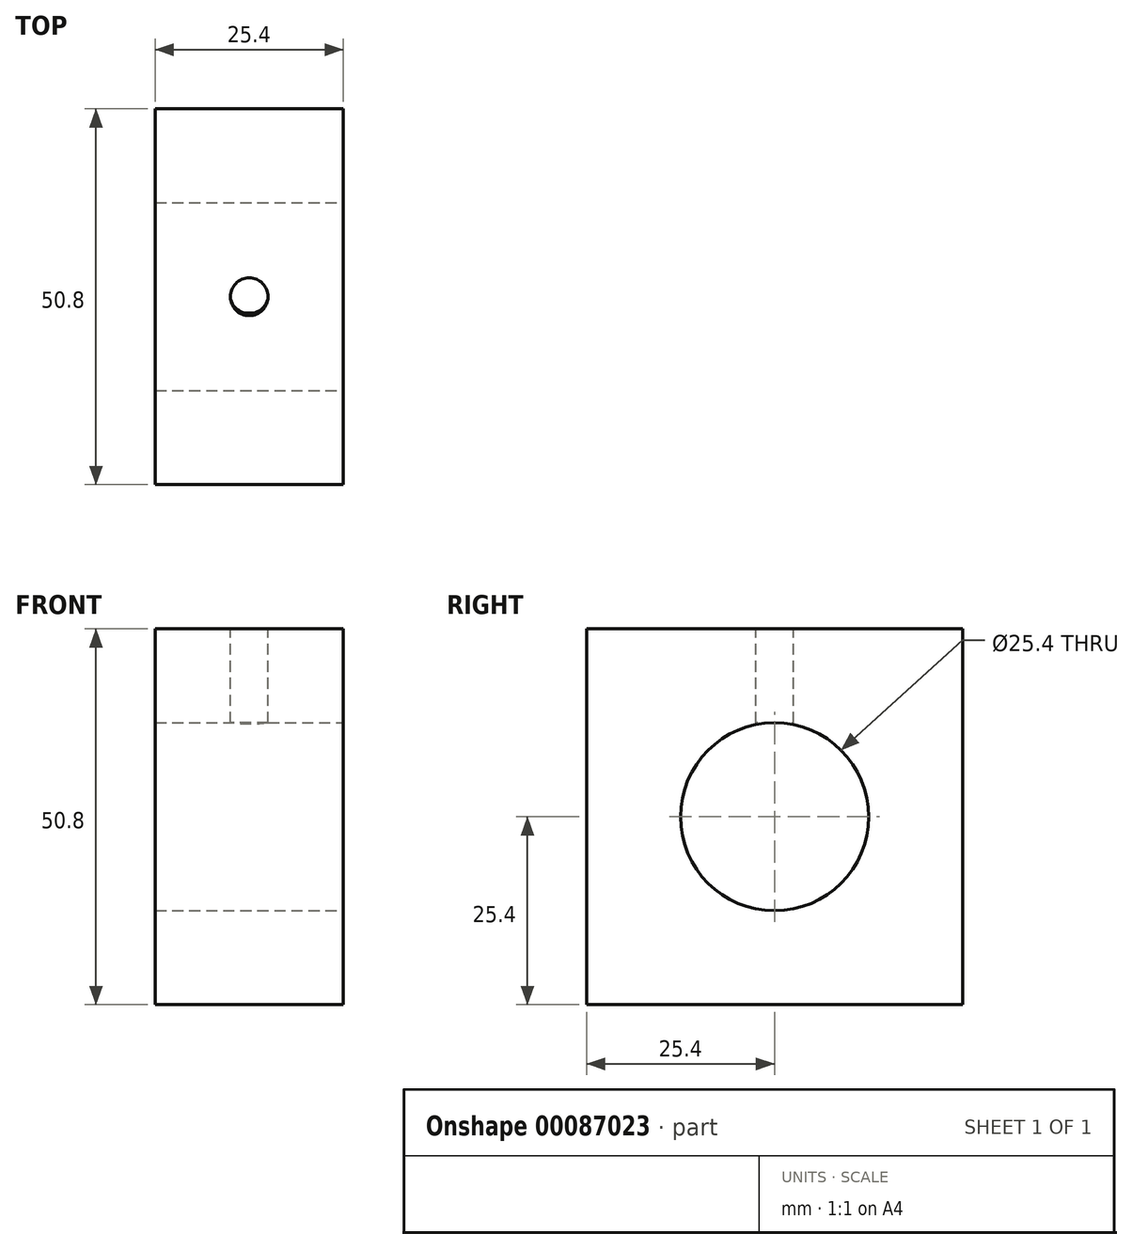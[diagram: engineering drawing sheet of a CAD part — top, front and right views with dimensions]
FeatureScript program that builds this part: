
annotation { "Feature Type Name" : "Feature", "Feature Type Description" : "" }
export const myFeature = defineFeature(function(context is Context, id is Id, definition is map)
    precondition{}
    {
        {
            var Q0;
            Q0=qCreatedBy(makeId("Front.planeOp"),FACE);
            var sketch = newSketch(context, id + "F0", { "sketchPlane" : qUnion([Q0])});
            skLineSegment(sketch, "E0.bottom", {"start": v(0, 0) * mm, "end": v(25.4, 0) * mm});
            skLineSegment(sketch, "E0.top", {"start": v(0, 50.8) * mm, "end": v(25.4, 50.8) * mm});
            skLineSegment(sketch, "E0.left", {"start": v(0, 0) * mm, "end": v(0, 50.8) * mm});
            skLineSegment(sketch, "E0.right", {"start": v(25.4, 0) * mm, "end": v(25.4, 50.8) * mm});
            skSolve(sketch);
        }
        {
            var Q0;
            Q0 = qSketchRegion(id + "F0", true);
            extrude(context, id + "F1", {"entities" : qUnion([Q0]), "depth" : 50.8 * mm});
        }
        {
            var Q0;
            Q0=makeQuery(id+"F1.opExtrude","SWEPT_FACE",FACE,{"disambiguationData":[OSD([sQuery(id+"F0.wireOp",EDGE,"E0.right")])]});
            var sketch = newSketch(context, id + "F2", { "sketchPlane" : qUnion([Q0])});
            skCircle(sketch, "E1", {"center": v(-25.4, 25.4) * mm, "radius": 12.7 * mm});
            skSolve(sketch);
        }
        {
            var Q0;
            Q0 = qSketchRegion(id + "F2", true);
            var Q1;
            Q1=makeQuery(id+"F1.opExtrude","SWEPT_FACE",FACE,{"disambiguationData":[OSD([sQuery(id+"F0.wireOp",EDGE,"E0.left")])]});
            extrude(context, id + "F3", {"entities" : qUnion([Q0]), "operationType" : NewBodyOperationType.REMOVE, "endBound" : BoundingType.THROUGH_ALL, "oppositeDirection" : true, "endBoundEntityFace" : qUnion([Q1]), "depth" : 25.4 * mm});
        }
        {
            var Q0;
            Q0=makeQuery(id+"F1.opExtrude","SWEPT_FACE",FACE,{"disambiguationData":[OSD([sQuery(id+"F0.wireOp",EDGE,"E0.top")])]});
            var sketch = newSketch(context, id + "F4", { "sketchPlane" : qUnion([Q0])});
            skPoint(sketch, "E2", {"position": v(12.7, -25.4) * mm});
            skPoint(sketch, "E3", {"position": v(12.7, -50.8) * mm});
            skSolve(sketch);
        }
        {
            var Q0;
            Q0=sQuery(id+"F4.wireOp",VERTEX,"E2");
            var Q1;
            Q1=makeQuery(id+"F1.opExtrude","SWEPT_BODY",BODY,{"disambiguationData":[OSD([sQuery(id+"F0.wireOp",EDGE,"E0.bottom"),sQuery(id+"F0.wireOp",EDGE,"E0.top"),sQuery(id+"F0.wireOp",EDGE,"E0.left"),sQuery(id+"F0.wireOp",EDGE,"E0.right")])]});
            hole(context, id + "F5", {"style" : HoleStyle.SIMPLE, "endStyle" : HoleEndStyle.BLIND, "standardTappedOrClearance" : lookupTablePath({ "standard" : "ANSI", "engagement" : "75%", "pitch" : "20 tpi", "size" : "1/4", "type" : "Tapped" }), "standardBlindInLast" : lookupTablePath({ "standard" : "ANSI", "engagement" : "75%", "pitch" : "20 tpi", "size" : "1/4", "type" : "Tapped" }), "holeDiameter" : 5.1 * mm, "holeDepth" : 12.7 * mm, "locations" : qUnion([Q0]), "scope" : qUnion([Q1]), "majorDiameter" : 6.35 * mm});
        }
    });
